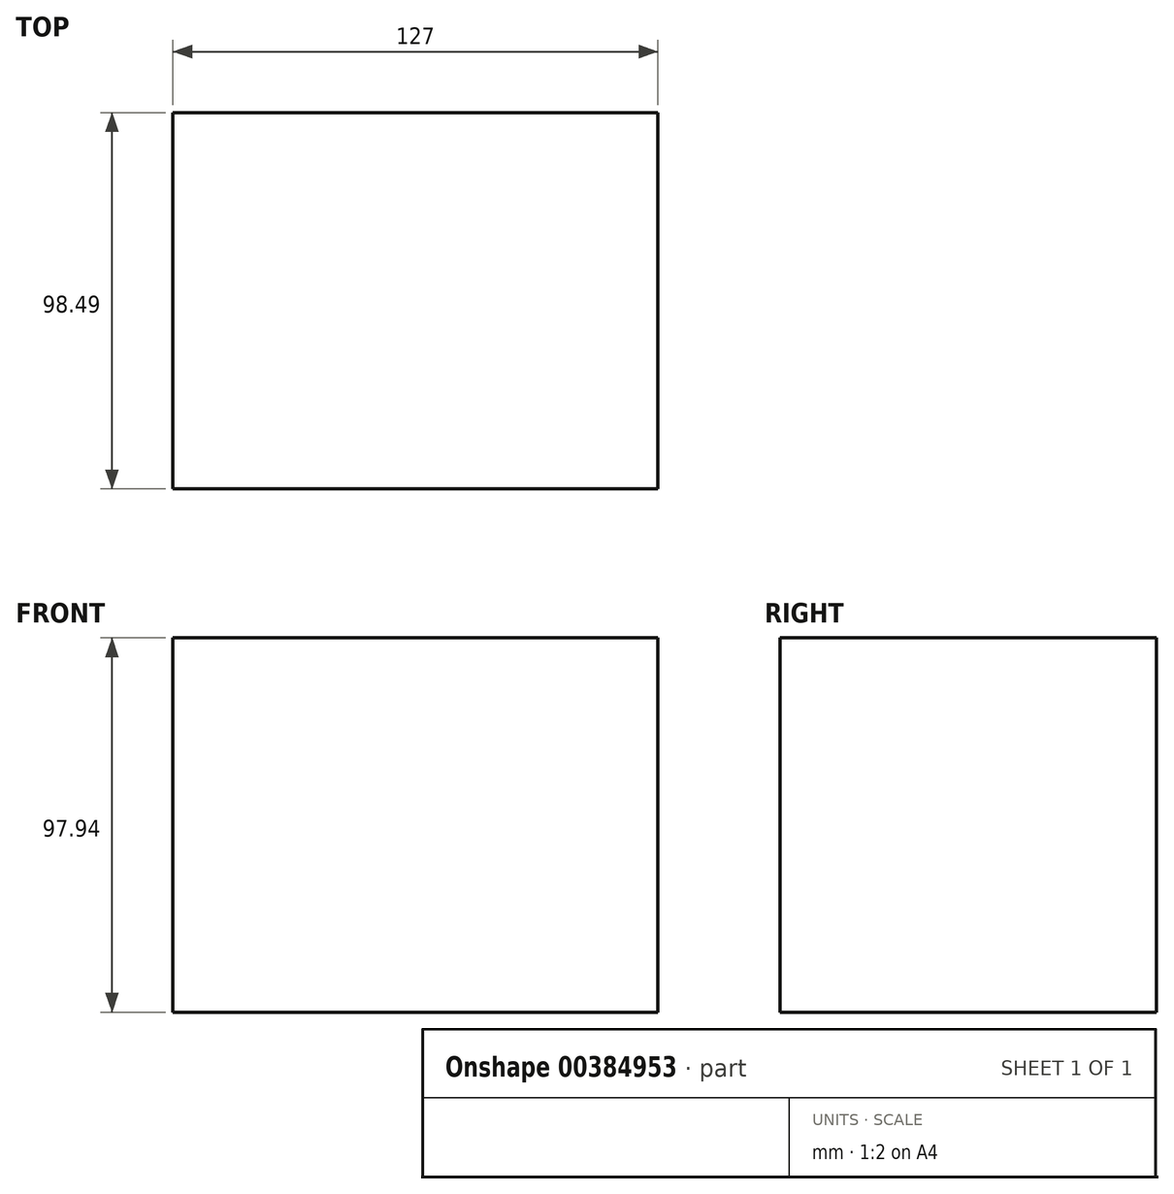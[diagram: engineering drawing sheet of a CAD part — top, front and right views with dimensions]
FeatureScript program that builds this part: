
annotation { "Feature Type Name" : "Feature", "Feature Type Description" : "" }
export const myFeature = defineFeature(function(context is Context, id is Id, definition is map)
    precondition{}
    {
        {
            var Q0;
            Q0=qCreatedBy(makeId("Right.planeOp"),FACE);
            var sketch = newSketch(context, id + "F0", { "sketchPlane" : qUnion([Q0])});
            skLineSegment(sketch, "E0.bottom", {"start": v(27.79, 20.47) * mm, "end": v(-70.7, 20.47) * mm});
            skLineSegment(sketch, "E0.top", {"start": v(27.79, -77.47) * mm, "end": v(-70.7, -77.47) * mm});
            skLineSegment(sketch, "E0.left", {"start": v(27.79, 20.47) * mm, "end": v(27.79, -77.47) * mm});
            skLineSegment(sketch, "E0.right", {"start": v(-70.7, 20.47) * mm, "end": v(-70.7, -77.47) * mm});
            skSolve(sketch);
        }
        {
            var Q0;
            Q0=makeQuery(id+"F0.imprint","IMPRINT",FACE,{"disambiguationData":[TD([[makeQuery(id+"F0.imprint","IMPRINT",EDGE,{"derivedFrom":sQuery(id+"F0.wireOp",EDGE,"E0.bottom")}),1.0]])]});
            extrude(context, id + "F1", {"entities" : qUnion([Q0]), "depth" : 127 * mm});
        }
    });
